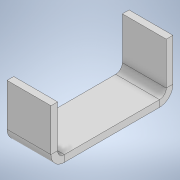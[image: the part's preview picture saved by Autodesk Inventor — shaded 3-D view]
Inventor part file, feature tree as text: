
AUTODESK INVENTOR PART (.ipt)
format: ipt  version: 2022 (Build 260153000, 153)  size: 136,704 bytes
history: native  units: in
note: dims shown in document units (in); Inventor stores cm internally (conversion verified against a paired STEP export)
features: sheet_metal_op x7, sketch x3, other x3
ambient origin geometry x8: Origin, YZ Plane, XZ Plane, XY Plane, X Axis, Y Axis, Z Axis, Center Point
bodies: Solid1 (feature_tree)
feature tree (13):
  sheet_metal_op  "Face1"
  sheet_metal_op  "Flange1"
  sheet_metal_op  "Flange2"
  sketch  "Sketch1"  dims[d0=2.189in]
  other  "Plate1"
  sketch  "Sketch2"  dims[d1=0.7874in]
  other  "Plate2"
  sheet_metal_op  "Bend1"
  sheet_metal_op  "Corner1"
  sketch  "Sketch3"  dims[d2=0.12in d3=0.12in d4=0.06in d5=0.24in d6=0.12in d7=1.0in d8=90.0deg d9=0.12in d10=0.48in d11=0.12in d12=0.12in d13=0.12in d14=0.06in d15=0.24in d16=0.12in d17=1.0in d18=90.0deg d19=0.12in d20=0.48in d21=0.12in d22=0.12in]
  other  "Plate3"
  sheet_metal_op  "Bend2"
  sheet_metal_op  "Corner2"
